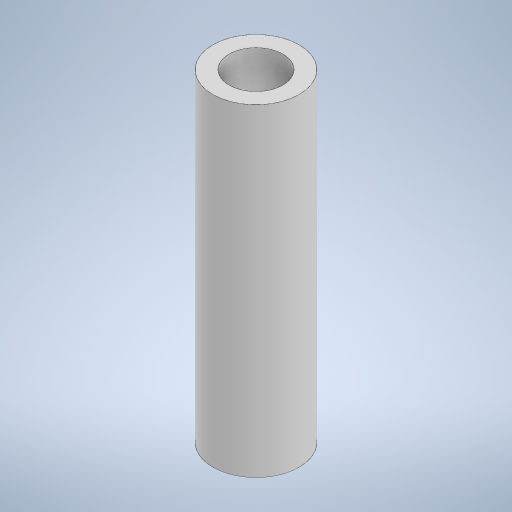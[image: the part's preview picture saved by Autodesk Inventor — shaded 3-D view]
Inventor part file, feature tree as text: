
AUTODESK INVENTOR PART (.ipt)
format: ipt  version: 2024.2 (Build 282272000, 272)  size: 219,136 bytes
history: native  units: in
note: dims shown in document units (in); Inventor stores cm internally (conversion verified against a paired STEP export)
features: extrude x1, sketch x1
ambient origin geometry x8: Origin, YZ Plane, XZ Plane, XY Plane, X Axis, Y Axis, Z Axis, Center Point
bodies: Solid1 (feature_tree)
feature tree (2):
  extrude  "Extrusion1"  Depth=0.6in
  sketch  "Sketch1"  dims[d0=0.1in d1=0.16in d2=0.6in d3=0.0in]
